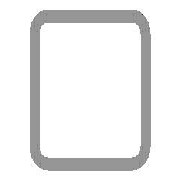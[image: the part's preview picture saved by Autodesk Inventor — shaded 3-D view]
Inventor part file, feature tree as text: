
AUTODESK INVENTOR PART (.ipt)
format: ipt  version: 2025 (Build 290162010, 162A)  size: 132,608 bytes
history: native  units: mm (DEFAULTED — no unit token found)
features: other x4, sketch x1, plane x1
ambient origin geometry x8: Origin, YZ Plane, XZ Plane, XY Plane, X Axis, Y Axis, Z Axis, Center Point
bodies: Solid1 (feature_tree), Body (feature_tree)
feature tree (6):
  parser-record x1  (decoder bookkeeping rows leaked as tree rows — omitted from the tree; the rows remain in map.json)
  other  "Driven Length"
  other  "Start Plane"
  other  "End Plane"
  sketch  "Sketch3"  dims[d3=606.743656mm d4=0.0mm d7=6.0mm d9=50.0mm d11=50.0mm d12=3.0mm d13=-0.0mm d14=606.743656mm d15=25.0mm d16=25.0mm d17=90.0deg d18=606.743656mm]
  plane  "Work Plane3"
